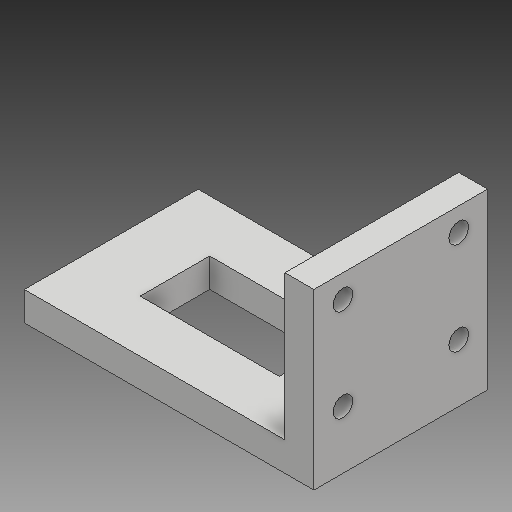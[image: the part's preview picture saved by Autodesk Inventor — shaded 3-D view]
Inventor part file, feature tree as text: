
AUTODESK INVENTOR PART (.ipt)
format: ipt  version: 2018 (Build 220112000, 112)  size: 114,688 bytes
history: native  units: mm
features: sketch x4, other x3
ambient origin geometry x8: Origin, YZ Plane, XZ Plane, XY Plane, X Axis, Y Axis, Z Axis, Center Point
bodies: Volumenkörper1 (feature_tree)
feature tree (7):
  other  "L-Halterung Servo.ipt"
  other  "Volumenkörper1::L-Halterung Servo.ipt"
  other  "Bezeichnung1"
  sketch  "Skizze1"  dims[d0=10.0mm]
  sketch  "Skizze2"
  sketch  "Skizze3"
  sketch  "Skizze4"
